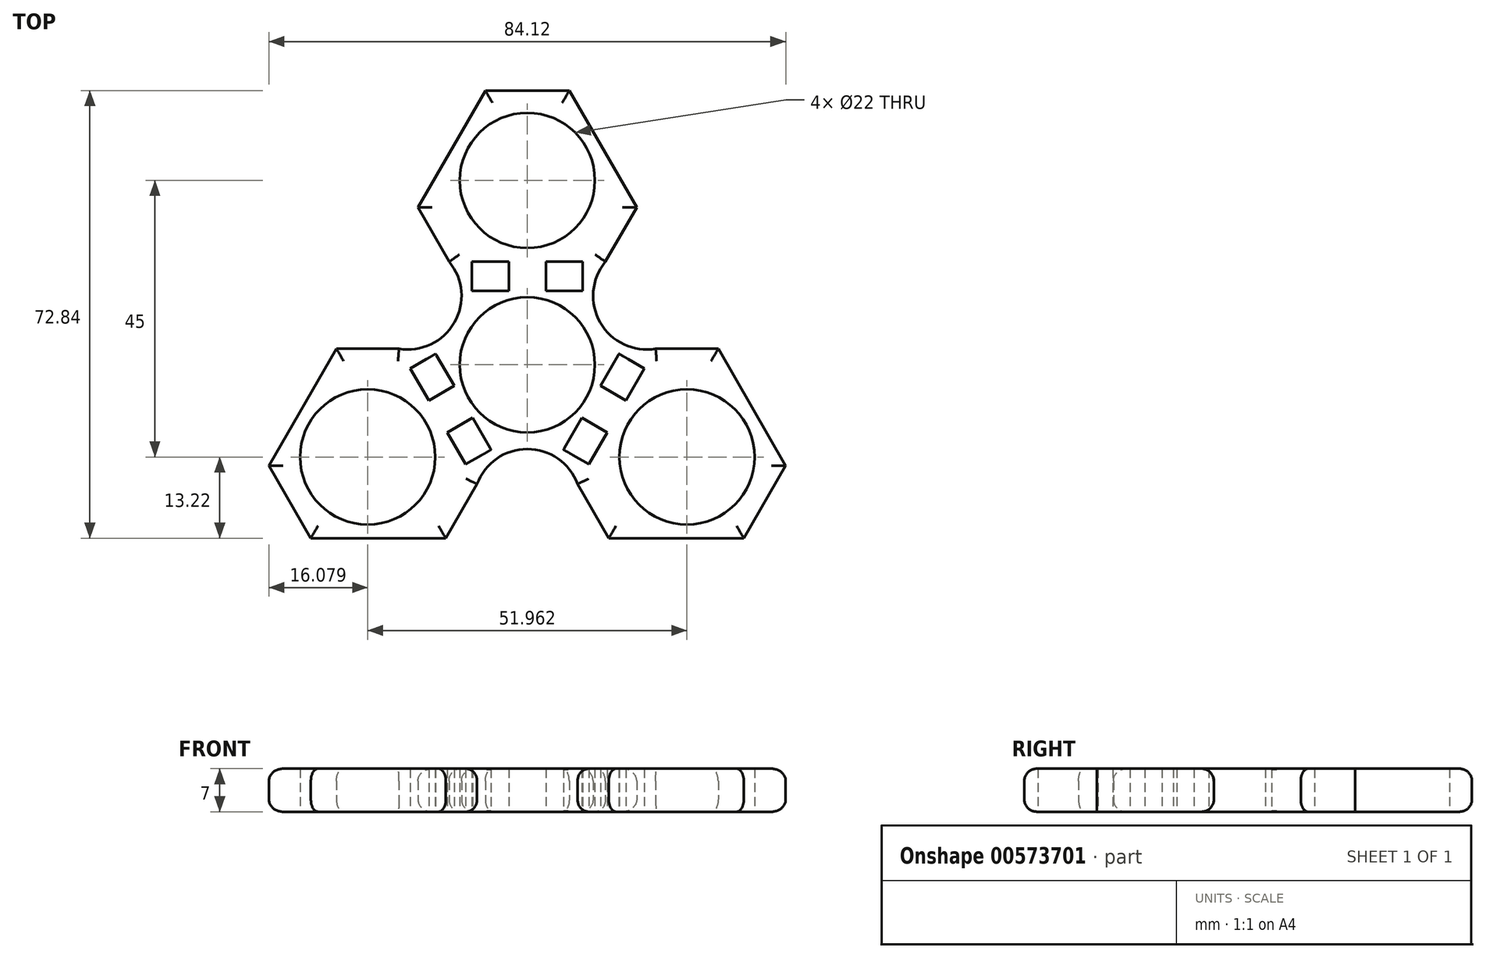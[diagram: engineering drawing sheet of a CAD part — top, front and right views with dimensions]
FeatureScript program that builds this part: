
annotation { "Feature Type Name" : "Feature", "Feature Type Description" : "" }
export const myFeature = defineFeature(function(context is Context, id is Id, definition is map)
    precondition{}
    {
        {
            var Q0;
            Q0=qCreatedBy(makeId("Top.planeOp"),FACE);
            var sketch = newSketch(context, id + "F0", { "sketchPlane" : qUnion([Q0])});
            skCircle(sketch, "E0", {"center": v(0, 0) * mm, "radius": 11 * mm});
            skLineSegment(sketch, "E1", {"start": v(0, 0) * mm, "end": v(0, 30) * mm});
            skCircle(sketch, "E2", {"center": v(0, 30) * mm, "radius": 11 * mm});
            skLineSegment(sketch, "E3.2.0", {"start": v(0, 0) * mm, "end": v(25.98, -15) * mm});
            skLineSegment(sketch, "E4", {"start": v(10.74, 12.02) * mm, "end": v(6.01, 12.02) * mm});
            skLineSegment(sketch, "E5.1.0", {"start": v(-15.78, 3.3) * mm, "end": v(-5.04, -15.31) * mm});
            skLineSegment(sketch, "E5.2.0", {"start": v(5.04, -15.31) * mm, "end": v(15.78, 3.3) * mm});
            skPoint(sketch, "E6", {"position": v(0, 15) * mm});
            skLineSegment(sketch, "E7", {"start": v(0, 12.02) * mm, "end": v(-6.01, 12.02) * mm});
            skPoint(sketch, "E8", {"position": v(-6.01, 12.02) * mm});
            skPoint(sketch, "E9", {"position": v(6.01, 12.02) * mm});
            skLineSegment(sketch, "E10", {"start": v(-6.01, 12.02) * mm, "end": v(-10.74, 12.02) * mm});
            skLineSegment(sketch, "E11", {"start": v(6.01, 12.02) * mm, "end": v(0, 12.02) * mm});
            skPoint(sketch, "E12", {"position": v(-3, 12.02) * mm});
            skPoint(sketch, "E13", {"position": v(-9.02, 12.02) * mm});
            skPoint(sketch, "E14", {"position": v(3, 12.02) * mm});
            skPoint(sketch, "E15", {"position": v(9.02, 12.02) * mm});
            skLineSegment(sketch, "E16", {"start": v(-3, 12.02) * mm, "end": v(-3, 17.98) * mm});
            skLineSegment(sketch, "E17", {"start": v(-9.02, 12.02) * mm, "end": v(-9.02, 17.98) * mm});
            skLineSegment(sketch, "E18.MirrorCS", {"start": v(3, 12.02) * mm, "end": v(3, 17.98) * mm});
            skLineSegment(sketch, "E19.MirrorCS", {"start": v(9.02, 12.02) * mm, "end": v(9.02, 17.98) * mm});
            skPoint(sketch, "E20", {"position": v(14.22, 8.21) * mm});
            skLineSegment(sketch, "E21.2.0", {"start": v(6.82, 44.62) * mm, "end": v(17.8, 25.6) * mm});
            skLineSegment(sketch, "E21.2.1", {"start": v(12.71, 16.78) * mm, "end": v(0, 16.78) * mm});
            skLineSegment(sketch, "E21.2.2", {"start": v(17.8, 25.6) * mm, "end": v(12.71, 16.78) * mm});
            skLineSegment(sketch, "E21.2.3", {"start": v(0, 16.78) * mm, "end": v(-12.71, 16.78) * mm});
            skLineSegment(sketch, "E21.2.4", {"start": v(-17.8, 25.6) * mm, "end": v(-12.71, 16.78) * mm});
            skLineSegment(sketch, "E21.2.5", {"start": v(-17.8, 25.6) * mm, "end": v(-6.82, 44.62) * mm});
            skLineSegment(sketch, "E22", {"start": v(-11.87, 6.86) * mm, "end": v(0, 0) * mm});
            skLineSegment(sketch, "E23.1.0", {"start": v(-13.27, -28.22) * mm, "end": v(-8.17, -19.4) * mm});
            skLineSegment(sketch, "E23.1.1", {"start": v(-13.27, -28.22) * mm, "end": v(-35.23, -28.22) * mm});
            skLineSegment(sketch, "E23.1.3", {"start": v(-42.06, -16.4) * mm, "end": v(-31.07, 2.62) * mm});
            skLineSegment(sketch, "E23.1.4", {"start": v(-31.07, 2.62) * mm, "end": v(-20.89, 2.62) * mm});
            skLineSegment(sketch, "E23.1.5", {"start": v(-20.89, 2.62) * mm, "end": v(-14.53, -8.39) * mm});
            skLineSegment(sketch, "E23.1.6", {"start": v(-14.53, -8.39) * mm, "end": v(-8.17, -19.4) * mm});
            skLineSegment(sketch, "E23.2.0", {"start": v(31.07, 2.62) * mm, "end": v(20.89, 2.62) * mm});
            skLineSegment(sketch, "E23.2.1", {"start": v(31.07, 2.62) * mm, "end": v(42.06, -16.4) * mm});
            skLineSegment(sketch, "E23.2.3", {"start": v(35.23, -28.22) * mm, "end": v(13.27, -28.22) * mm});
            skLineSegment(sketch, "E23.2.4", {"start": v(13.27, -28.22) * mm, "end": v(8.17, -19.4) * mm});
            skLineSegment(sketch, "E23.2.5", {"start": v(8.17, -19.4) * mm, "end": v(14.53, -8.39) * mm});
            skLineSegment(sketch, "E23.2.6", {"start": v(14.53, -8.39) * mm, "end": v(20.89, 2.62) * mm});
            skArc(sketch, "E24", {"start": v(-20.89, 2.62) * mm, "mid": v(-11.87, 6.86) * mm, "end": v(-12.71, 16.78) * mm});
            skPoint(sketch, "E25.orphan", {"position": v(-16.42, 4.4) * mm});
            skPoint(sketch, "E26.orphan", {"position": v(-12.02, 12.02) * mm});
            skLineSegment(sketch, "E27.1.0", {"start": v(-8.9, -8.61) * mm, "end": v(-14.07, -11.6) * mm});
            skLineSegment(sketch, "E27.1.1", {"start": v(-5.9, -13.82) * mm, "end": v(-11.06, -16.8) * mm});
            skLineSegment(sketch, "E27.1.2", {"start": v(-11.91, -3.4) * mm, "end": v(-17.07, -6.39) * mm});
            skLineSegment(sketch, "E27.1.3", {"start": v(-14.92, 1.8) * mm, "end": v(-20.08, -1.18) * mm});
            skArc(sketch, "E27.1.4", {"start": v(8.17, -19.4) * mm, "mid": v(0, -13.71) * mm, "end": v(-8.17, -19.4) * mm});
            skCircle(sketch, "E27.1.5", {"center": v(-25.98, -15) * mm, "radius": 11 * mm});
            skLineSegment(sketch, "E27.2.0", {"start": v(11.91, -3.4) * mm, "end": v(17.07, -6.39) * mm});
            skLineSegment(sketch, "E27.2.1", {"start": v(14.92, 1.8) * mm, "end": v(20.08, -1.18) * mm});
            skLineSegment(sketch, "E27.2.2", {"start": v(8.9, -8.61) * mm, "end": v(14.07, -11.6) * mm});
            skLineSegment(sketch, "E27.2.3", {"start": v(5.9, -13.82) * mm, "end": v(11.06, -16.8) * mm});
            skArc(sketch, "E27.2.4", {"start": v(12.71, 16.78) * mm, "mid": v(11.87, 6.86) * mm, "end": v(20.89, 2.62) * mm});
            skCircle(sketch, "E27.2.5", {"center": v(25.98, -15) * mm, "radius": 11 * mm});
            skPoint(sketch, "E28.orphan", {"position": v(-4.4, -16.42) * mm});
            skPoint(sketch, "E29.orphan", {"position": v(4.4, -16.42) * mm});
            skPoint(sketch, "E30.orphan", {"position": v(12.02, 12.02) * mm});
            skPoint(sketch, "E31.orphan", {"position": v(16.42, 4.4) * mm});
            skLineSegment(sketch, "E32.0", {"start": v(-5.1, 44.62) * mm, "end": v(5.1, 44.62) * mm});
            skLineSegment(sketch, "E33", {"start": v(5.1, 44.62) * mm, "end": v(6.82, 44.62) * mm});
            skLineSegment(sketch, "E34", {"start": v(-5.1, 44.62) * mm, "end": v(-6.82, 44.62) * mm});
            skLineSegment(sketch, "E35.1.0", {"start": v(-36.1, -26.72) * mm, "end": v(-41.19, -17.9) * mm});
            skLineSegment(sketch, "E35.1.1", {"start": v(-36.1, -26.72) * mm, "end": v(-35.23, -28.22) * mm});
            skLineSegment(sketch, "E35.1.2", {"start": v(-41.19, -17.9) * mm, "end": v(-42.06, -16.4) * mm});
            skLineSegment(sketch, "E35.2.0", {"start": v(41.19, -17.9) * mm, "end": v(36.1, -26.72) * mm});
            skLineSegment(sketch, "E35.2.1", {"start": v(41.19, -17.9) * mm, "end": v(42.06, -16.4) * mm});
            skLineSegment(sketch, "E35.2.2", {"start": v(36.1, -26.72) * mm, "end": v(35.23, -28.22) * mm});
            skPoint(sketch, "E36.orphan", {"position": v(-43.79, -19.4) * mm});
            skPoint(sketch, "E37.orphan", {"position": v(-38.7, -28.22) * mm});
            skPoint(sketch, "E38.orphan", {"position": v(43.79, -19.4) * mm});
            skPoint(sketch, "E39.orphan", {"position": v(5.1, 47.62) * mm});
            skPoint(sketch, "E40.orphan", {"position": v(-5.1, 47.62) * mm});
            skSolve(sketch);
        }
        {
            var Q0;
            Q0=makeQuery(id+"F0.imprint","IMPRINT",FACE,{"disambiguationData":[TD([[makeQuery(id+"F0.imprint","IMPRINT",EDGE,{"derivedFrom":sQuery(id+"F0.wireOp",EDGE,"E2")}),-1.0]])]});
            var Q1;
            {var subQ0=sQuery(id+"F0.wireOp",EDGE,"E24");var subQ1=sQuery(id+"F0.wireOp",EDGE,"E10");var subQ2=makeQuery(id+"F0.imprint","INTERSECT",VERTEX,{"derivedFrom":[subQ1,subQ0]});Q1=makeQuery(id+"F0.imprint","IMPRINT",FACE,{"disambiguationData":[TD([[makeQuery(id+"F0.imprint","IMPRINT",EDGE,{"disambiguationData":[TD([[subQ2,1.0]])],"derivedFrom":subQ1}),-1.0]])]});}
            var Q2;
            {var subQ6=sQuery(id+"F0.wireOp",EDGE,"E0");var subQ11=sQuery(id+"F0.wireOp",EDGE,"E22");var subQ13=makeQuery(id+"F0.imprint","INTERSECT",VERTEX,{"derivedFrom":[subQ6,subQ11]});Q2=makeQuery(id+"F0.imprint","IMPRINT",FACE,{"disambiguationData":[TD([[makeQuery(id+"F0.imprint","IMPRINT",EDGE,{"disambiguationData":[TD([[subQ13,1.0]])],"derivedFrom":subQ6}),-1.0]])]});}
            var Q3;
            {var subQ1=sQuery(id+"F0.wireOp",EDGE,"E1");var subQ6=sQuery(id+"F0.wireOp",EDGE,"E0");var subQ7=makeQuery(id+"F0.imprint","INTERSECT",VERTEX,{"derivedFrom":[subQ6,subQ1]});Q3=makeQuery(id+"F0.imprint","IMPRINT",FACE,{"disambiguationData":[TD([[makeQuery(id+"F0.imprint","IMPRINT",EDGE,{"disambiguationData":[TD([[subQ7,1.0]])],"derivedFrom":subQ6}),-1.0]])]});}
            var Q4;
            {var subQ12=sQuery(id+"F0.wireOp",EDGE,"E0");var subQ15=sQuery(id+"F0.wireOp",EDGE,"E22");var subQ16=makeQuery(id+"F0.imprint","INTERSECT",VERTEX,{"derivedFrom":[subQ12,subQ15]});Q4=makeQuery(id+"F0.imprint","IMPRINT",FACE,{"disambiguationData":[TD([[makeQuery(id+"F0.imprint","IMPRINT",EDGE,{"disambiguationData":[TD([[subQ16,-1.0]])],"derivedFrom":subQ12}),-1.0]])]});}
            var Q5;
            {var subQ0=sQuery(id+"F0.wireOp",EDGE,"E7");var subQ5=sQuery(id+"F0.wireOp",EDGE,"E16");var subQ6=makeQuery(id+"F0.imprint","INTERSECT",VERTEX,{"derivedFrom":[subQ0,subQ5]});Q5=makeQuery(id+"F0.imprint","IMPRINT",FACE,{"disambiguationData":[TD([[makeQuery(id+"F0.imprint","IMPRINT",EDGE,{"disambiguationData":[TD([[subQ6,-1.0]])],"derivedFrom":subQ5}),-1.0]])]});}
            var Q6;
            {var subQ0=sQuery(id+"F0.wireOp",EDGE,"E11");var subQ5=sQuery(id+"F0.wireOp",EDGE,"E18.MirrorCS");var subQ6=makeQuery(id+"F0.imprint","INTERSECT",VERTEX,{"derivedFrom":[subQ0,subQ5]});Q6=makeQuery(id+"F0.imprint","IMPRINT",FACE,{"disambiguationData":[TD([[makeQuery(id+"F0.imprint","IMPRINT",EDGE,{"disambiguationData":[TD([[subQ6,-1.0]])],"derivedFrom":subQ5}),1.0]])]});}
            var Q7;
            {var subQ0=sQuery(id+"F0.wireOp",EDGE,"E27.2.4");var subQ1=sQuery(id+"F0.wireOp",EDGE,"E4");var subQ2=makeQuery(id+"F0.imprint","INTERSECT",VERTEX,{"derivedFrom":[subQ1,subQ0]});Q7=makeQuery(id+"F0.imprint","IMPRINT",FACE,{"disambiguationData":[TD([[makeQuery(id+"F0.imprint","IMPRINT",EDGE,{"disambiguationData":[TD([[subQ2,-1.0]])],"derivedFrom":subQ1}),-1.0]])]});}
            var Q8;
            {var subQ0=sQuery(id+"F0.wireOp",EDGE,"E24");var subQ1=sQuery(id+"F0.wireOp",EDGE,"E5.1.0");var subQ2=makeQuery(id+"F0.imprint","INTERSECT",VERTEX,{"derivedFrom":[subQ1,subQ0]});Q8=makeQuery(id+"F0.imprint","IMPRINT",FACE,{"disambiguationData":[TD([[makeQuery(id+"F0.imprint","IMPRINT",EDGE,{"disambiguationData":[TD([[subQ2,-1.0]])],"derivedFrom":subQ1}),-1.0]])]});}
            var Q9;
            {var subQ0=sQuery(id+"F0.wireOp",EDGE,"E27.1.0");var subQ1=sQuery(id+"F0.wireOp",EDGE,"E5.1.0");var subQ2=makeQuery(id+"F0.imprint","INTERSECT",VERTEX,{"derivedFrom":[subQ1,subQ0]});Q9=makeQuery(id+"F0.imprint","IMPRINT",FACE,{"disambiguationData":[TD([[makeQuery(id+"F0.imprint","IMPRINT",EDGE,{"disambiguationData":[TD([[subQ2,1.0]])],"derivedFrom":subQ1}),-1.0]])]});}
            var Q10;
            {var subQ0=sQuery(id+"F0.wireOp",EDGE,"E27.1.4");var subQ1=sQuery(id+"F0.wireOp",EDGE,"E5.1.0");var subQ2=makeQuery(id+"F0.imprint","INTERSECT",VERTEX,{"derivedFrom":[subQ1,subQ0]});Q10=makeQuery(id+"F0.imprint","IMPRINT",FACE,{"disambiguationData":[TD([[makeQuery(id+"F0.imprint","IMPRINT",EDGE,{"disambiguationData":[TD([[subQ2,1.0]])],"derivedFrom":subQ1}),-1.0]])]});}
            var Q11;
            {var subQ8=sQuery(id+"F0.wireOp",EDGE,"E23.1.0");Q11=makeQuery(id+"F0.imprint","IMPRINT",FACE,{"disambiguationData":[TD([[makeQuery(id+"F0.imprint","IMPRINT",EDGE,{"derivedFrom":subQ8}),1.0]])]});}
            var Q12;
            {var subQ0=sQuery(id+"F0.wireOp",EDGE,"E27.1.4");var subQ1=sQuery(id+"F0.wireOp",EDGE,"E5.2.0");var subQ2=makeQuery(id+"F0.imprint","INTERSECT",VERTEX,{"derivedFrom":[subQ1,subQ0]});Q12=makeQuery(id+"F0.imprint","IMPRINT",FACE,{"disambiguationData":[TD([[makeQuery(id+"F0.imprint","IMPRINT",EDGE,{"disambiguationData":[TD([[subQ2,-1.0]])],"derivedFrom":subQ1}),-1.0]])]});}
            var Q13;
            {var subQ3=sQuery(id+"F0.wireOp",EDGE,"E5.2.0");var subQ5=sQuery(id+"F0.wireOp",EDGE,"E27.2.2");var subQ6=makeQuery(id+"F0.imprint","INTERSECT",VERTEX,{"derivedFrom":[subQ3,subQ5]});Q13=makeQuery(id+"F0.imprint","IMPRINT",FACE,{"disambiguationData":[TD([[makeQuery(id+"F0.imprint","IMPRINT",EDGE,{"disambiguationData":[TD([[subQ6,-1.0]])],"derivedFrom":subQ3}),-1.0]])]});}
            var Q14;
            {var subQ3=sQuery(id+"F0.wireOp",EDGE,"E5.2.0");var subQ5=sQuery(id+"F0.wireOp",EDGE,"E27.2.0");var subQ6=makeQuery(id+"F0.imprint","INTERSECT",VERTEX,{"derivedFrom":[subQ3,subQ5]});Q14=makeQuery(id+"F0.imprint","IMPRINT",FACE,{"disambiguationData":[TD([[makeQuery(id+"F0.imprint","IMPRINT",EDGE,{"disambiguationData":[TD([[subQ6,1.0]])],"derivedFrom":subQ3}),-1.0]])]});}
            var Q15;
            {var subQ0=sQuery(id+"F0.wireOp",EDGE,"E27.2.4");var subQ1=sQuery(id+"F0.wireOp",EDGE,"E5.2.0");var subQ2=makeQuery(id+"F0.imprint","INTERSECT",VERTEX,{"derivedFrom":[subQ1,subQ0]});Q15=makeQuery(id+"F0.imprint","IMPRINT",FACE,{"disambiguationData":[TD([[makeQuery(id+"F0.imprint","IMPRINT",EDGE,{"disambiguationData":[TD([[subQ2,1.0]])],"derivedFrom":subQ1}),-1.0]])]});}
            var Q16;
            {var subQ8=sQuery(id+"F0.wireOp",EDGE,"E23.2.0");Q16=makeQuery(id+"F0.imprint","IMPRINT",FACE,{"disambiguationData":[TD([[makeQuery(id+"F0.imprint","IMPRINT",EDGE,{"derivedFrom":subQ8}),1.0]])]});}
            extrude(context, id + "F1", {"entities" : qUnion([Q0, Q1, Q2, Q3, Q4, Q5, Q6, Q7, Q8, Q9, Q10, Q11, Q12, Q13, Q14, Q15, Q16]), "depth" : 7 * mm, "offsetDistance" : 25 * mm});
        }
        {
            var Q0;
            Q0=makeQuery(id+"F1.opExtrude","CAP_EDGE",EDGE,{"disambiguationData":[OSD([sQuery(id+"F0.wireOp",EDGE,"E21.2.5")])],"isStart":false});
            var Q1;
            Q1=makeQuery(id+"F1.opExtrude","CAP_EDGE",EDGE,{"disambiguationData":[OSD([sQuery(id+"F0.wireOp",EDGE,"E32.0"),sQuery(id+"F0.wireOp",EDGE,"E33"),sQuery(id+"F0.wireOp",EDGE,"E34")])],"isStart":false});
            var Q2;
            Q2=makeQuery(id+"F1.opExtrude","CAP_EDGE",EDGE,{"disambiguationData":[OSD([sQuery(id+"F0.wireOp",EDGE,"E21.2.0")])],"isStart":false});
            var Q3;
            Q3=makeQuery(id+"F1.opExtrude","CAP_EDGE",EDGE,{"disambiguationData":[OSD([sQuery(id+"F0.wireOp",EDGE,"E21.2.2")])],"isStart":false});
            var Q4;
            Q4=makeQuery(id+"F1.opExtrude","CAP_EDGE",EDGE,{"disambiguationData":[OSD([sQuery(id+"F0.wireOp",EDGE,"E27.2.4")])],"isStart":false});
            var Q5;
            Q5=makeQuery(id+"F1.opExtrude","CAP_EDGE",EDGE,{"disambiguationData":[OSD([sQuery(id+"F0.wireOp",EDGE,"E23.2.0")])],"isStart":false});
            var Q6;
            Q6=makeQuery(id+"F1.opExtrude","CAP_EDGE",EDGE,{"disambiguationData":[OSD([sQuery(id+"F0.wireOp",EDGE,"E23.2.1")])],"isStart":false});
            var Q7;
            Q7=makeQuery(id+"F1.opExtrude","CAP_EDGE",EDGE,{"disambiguationData":[OSD([sQuery(id+"F0.wireOp",EDGE,"E35.2.0"),sQuery(id+"F0.wireOp",EDGE,"E35.2.1"),sQuery(id+"F0.wireOp",EDGE,"E35.2.2")])],"isStart":false});
            var Q8;
            Q8=makeQuery(id+"F1.opExtrude","CAP_EDGE",EDGE,{"disambiguationData":[OSD([sQuery(id+"F0.wireOp",EDGE,"E23.2.3")])],"isStart":false});
            var Q9;
            Q9=makeQuery(id+"F1.opExtrude","CAP_EDGE",EDGE,{"disambiguationData":[OSD([sQuery(id+"F0.wireOp",EDGE,"E23.2.4")])],"isStart":false});
            var Q10;
            Q10=makeQuery(id+"F1.opExtrude","CAP_EDGE",EDGE,{"disambiguationData":[OSD([sQuery(id+"F0.wireOp",EDGE,"E27.1.4")])],"isStart":false});
            var Q11;
            Q11=makeQuery(id+"F1.opExtrude","CAP_EDGE",EDGE,{"disambiguationData":[OSD([sQuery(id+"F0.wireOp",EDGE,"E23.1.0")])],"isStart":false});
            var Q12;
            Q12=makeQuery(id+"F1.opExtrude","CAP_EDGE",EDGE,{"disambiguationData":[OSD([sQuery(id+"F0.wireOp",EDGE,"E23.1.1")])],"isStart":false});
            var Q13;
            Q13=makeQuery(id+"F1.opExtrude","CAP_EDGE",EDGE,{"disambiguationData":[OSD([sQuery(id+"F0.wireOp",EDGE,"E35.1.0"),sQuery(id+"F0.wireOp",EDGE,"E35.1.1"),sQuery(id+"F0.wireOp",EDGE,"E35.1.2")])],"isStart":false});
            var Q14;
            Q14=makeQuery(id+"F1.opExtrude","CAP_EDGE",EDGE,{"disambiguationData":[OSD([sQuery(id+"F0.wireOp",EDGE,"E23.1.3")])],"isStart":false});
            var Q15;
            Q15=makeQuery(id+"F1.opExtrude","CAP_EDGE",EDGE,{"disambiguationData":[OSD([sQuery(id+"F0.wireOp",EDGE,"E23.1.4")])],"isStart":false});
            var Q16;
            Q16=makeQuery(id+"F1.opExtrude","CAP_EDGE",EDGE,{"disambiguationData":[OSD([sQuery(id+"F0.wireOp",EDGE,"E24")])],"isStart":false});
            var Q17;
            Q17=makeQuery(id+"F1.opExtrude","CAP_EDGE",EDGE,{"disambiguationData":[OSD([sQuery(id+"F0.wireOp",EDGE,"E21.2.4")])],"isStart":false});
            fillet(context, id + "F2", {"entities" : qUnion([Q0, Q1, Q2, Q3, Q4, Q5, Q6, Q7, Q8, Q9, Q10, Q11, Q12, Q13, Q14, Q15, Q16, Q17]), "radius" : 2 * mm, "tangentPropagation" : true, "allowEdgeOverflow" : false});
        }
        {
            var Q0;
            Q0=makeQuery(id+"F1.opExtrude","CAP_EDGE",EDGE,{"disambiguationData":[OSD([sQuery(id+"F0.wireOp",EDGE,"E23.1.1")])],"isStart":true});
            var Q1;
            Q1=makeQuery(id+"F1.opExtrude","CAP_EDGE",EDGE,{"disambiguationData":[OSD([sQuery(id+"F0.wireOp",EDGE,"E35.1.0"),sQuery(id+"F0.wireOp",EDGE,"E35.1.1"),sQuery(id+"F0.wireOp",EDGE,"E35.1.2")])],"isStart":true});
            var Q2;
            Q2=makeQuery(id+"F1.opExtrude","CAP_EDGE",EDGE,{"disambiguationData":[OSD([sQuery(id+"F0.wireOp",EDGE,"E23.1.3")])],"isStart":true});
            var Q3;
            Q3=makeQuery(id+"F1.opExtrude","CAP_EDGE",EDGE,{"disambiguationData":[OSD([sQuery(id+"F0.wireOp",EDGE,"E23.1.4")])],"isStart":true});
            var Q4;
            Q4=makeQuery(id+"F1.opExtrude","CAP_EDGE",EDGE,{"disambiguationData":[OSD([sQuery(id+"F0.wireOp",EDGE,"E24")])],"isStart":true});
            var Q5;
            Q5=makeQuery(id+"F1.opExtrude","CAP_EDGE",EDGE,{"disambiguationData":[OSD([sQuery(id+"F0.wireOp",EDGE,"E21.2.4")])],"isStart":true});
            var Q6;
            Q6=makeQuery(id+"F1.opExtrude","CAP_EDGE",EDGE,{"disambiguationData":[OSD([sQuery(id+"F0.wireOp",EDGE,"E21.2.5")])],"isStart":true});
            var Q7;
            Q7=makeQuery(id+"F1.opExtrude","CAP_EDGE",EDGE,{"disambiguationData":[OSD([sQuery(id+"F0.wireOp",EDGE,"E32.0"),sQuery(id+"F0.wireOp",EDGE,"E33"),sQuery(id+"F0.wireOp",EDGE,"E34")])],"isStart":true});
            var Q8;
            Q8=makeQuery(id+"F1.opExtrude","CAP_EDGE",EDGE,{"disambiguationData":[OSD([sQuery(id+"F0.wireOp",EDGE,"E21.2.0")])],"isStart":true});
            var Q9;
            Q9=makeQuery(id+"F1.opExtrude","CAP_EDGE",EDGE,{"disambiguationData":[OSD([sQuery(id+"F0.wireOp",EDGE,"E21.2.2")])],"isStart":true});
            var Q10;
            Q10=makeQuery(id+"F1.opExtrude","CAP_EDGE",EDGE,{"disambiguationData":[OSD([sQuery(id+"F0.wireOp",EDGE,"E27.2.4")])],"isStart":true});
            var Q11;
            Q11=makeQuery(id+"F1.opExtrude","CAP_EDGE",EDGE,{"disambiguationData":[OSD([sQuery(id+"F0.wireOp",EDGE,"E23.2.0")])],"isStart":true});
            var Q12;
            Q12=makeQuery(id+"F1.opExtrude","CAP_EDGE",EDGE,{"disambiguationData":[OSD([sQuery(id+"F0.wireOp",EDGE,"E23.2.1")])],"isStart":true});
            var Q13;
            Q13=makeQuery(id+"F1.opExtrude","CAP_EDGE",EDGE,{"disambiguationData":[OSD([sQuery(id+"F0.wireOp",EDGE,"E35.2.0"),sQuery(id+"F0.wireOp",EDGE,"E35.2.1"),sQuery(id+"F0.wireOp",EDGE,"E35.2.2")])],"isStart":true});
            var Q14;
            Q14=makeQuery(id+"F1.opExtrude","CAP_EDGE",EDGE,{"disambiguationData":[OSD([sQuery(id+"F0.wireOp",EDGE,"E23.2.3")])],"isStart":true});
            var Q15;
            Q15=makeQuery(id+"F1.opExtrude","CAP_EDGE",EDGE,{"disambiguationData":[OSD([sQuery(id+"F0.wireOp",EDGE,"E23.2.4")])],"isStart":true});
            var Q16;
            Q16=makeQuery(id+"F1.opExtrude","CAP_EDGE",EDGE,{"disambiguationData":[OSD([sQuery(id+"F0.wireOp",EDGE,"E27.1.4")])],"isStart":true});
            var Q17;
            Q17=makeQuery(id+"F1.opExtrude","CAP_EDGE",EDGE,{"disambiguationData":[OSD([sQuery(id+"F0.wireOp",EDGE,"E23.1.0")])],"isStart":true});
            fillet(context, id + "F3", {"entities" : qUnion([Q0, Q1, Q2, Q3, Q4, Q5, Q6, Q7, Q8, Q9, Q10, Q11, Q12, Q13, Q14, Q15, Q16, Q17]), "radius" : 2 * mm, "tangentPropagation" : true, "allowEdgeOverflow" : false});
        }
    });
